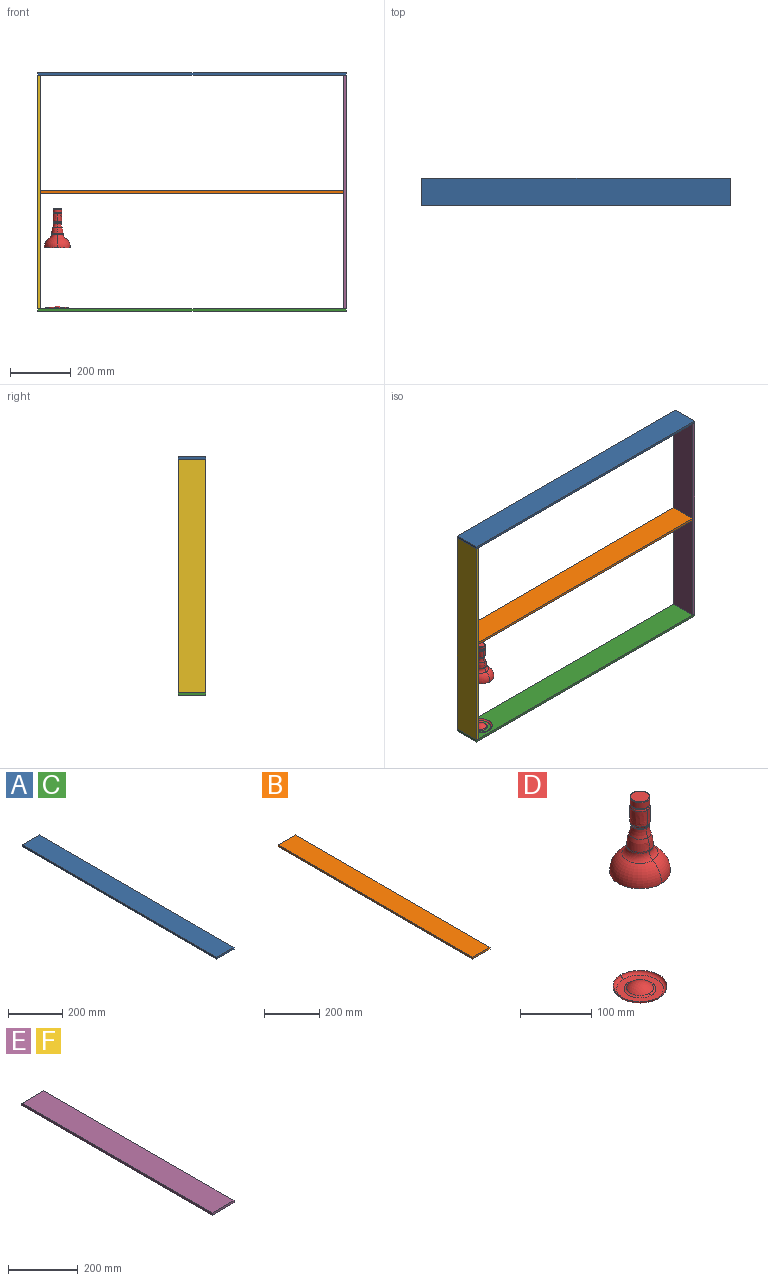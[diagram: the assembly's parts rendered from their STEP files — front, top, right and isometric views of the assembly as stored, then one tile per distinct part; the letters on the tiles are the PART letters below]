
ASSEMBLY  parts=6 mates=5
PART A: 6 faces, bbox 88.9x1016x7.9 mm
  f0: plane 1016x7.94mm, normal (-1,0,0), area 8064.5mm2, adj f1,f3,f4,f5
  f1: plane 88.9x7.94mm, normal (0,-1,0), area 705.6mm2, adj f0,f2,f4,f5
  f2: plane 1016x7.94mm, normal (1,0,0), area 8064.5mm2, adj f1,f3,f4,f5
  f3: plane 88.9x7.94mm, normal (0,1,0), area 705.6mm2, adj f0,f2,f4,f5
  f4: plane 1016x88.9mm, normal (0,0,1), area 90322.4mm2, adj f0,f1,f2,f3
  f5: plane 1016x88.9mm, normal (0,0,-1), area 90322.4mm2, adj f0,f1,f2,f3
PART B: 6 faces, bbox 88.9x1000.1x7.9 mm
  f0: plane 88.9x7.94mm, normal (0,-1,0), area 705.6mm2, adj f1,f3,f4,f5
  f1: plane 1000.13x7.94mm, normal (1,0,0), area 7938.5mm2, adj f0,f2,f4,f5
  f2: plane 88.9x7.94mm, normal (0,1,0), area 705.6mm2, adj f1,f3,f4,f5
  f3: plane 1000.13x7.94mm, normal (-1,0,0), area 7938.5mm2, adj f0,f2,f4,f5
  f4: plane 1000.13x88.9mm, normal (0,0,1), area 88911.1mm2, adj f0,f1,f2,f3
  f5: plane 1000.13x88.9mm, normal (0,0,-1), area 88911.1mm2, adj f0,f1,f2,f3
PART C: same geometry as A
PART D: 35 faces, bbox 84.8x84.9x333.9 mm
  f0: sphere r=25mm, area 833.3mm2, adj f1,f2
  f1: torus R=22.36mm, axis (0,0,1), area 269.2mm2, adj f0,f2,f3
  f2: torus R=22.36mm, axis (0,0,1), area 269.2mm2, adj f0,f1,f3
  f3: plane 65.68x65.68mm, normal (0,0,-1), area 1818.2mm2, adj f1,f2,f4,f5
  f4: torus R=32.84mm, axis (0,0,1), area 875mm2, adj f3,f5,f6
  f5: torus R=32.84mm, axis (0,0,1), area 875mm2, adj f3,f4,f6
  f6: cone r=0mm half-angle=1.3deg, axis (0,0,1), area 49622.5mm2, adj f4,f5,f7,f8
  f7: torus R=8.99mm, axis (0,0,1), area 4352mm2, adj f6,f8,f9
  f8: torus R=8.99mm, axis (0,0,1), area 4352mm2, adj f6,f7,f10
  f9: torus R=33.78mm, axis (0,0,1), area 970.6mm2, adj f7,f10,f11
  f10: torus R=33.78mm, axis (0,0,1), area 970.6mm2, adj f8,f9,f12
  f11: torus R=33.78mm, axis (0,0,1), area 134mm2, adj f9,f12,f13
  f12: torus R=33.78mm, axis (0,0,1), area 134mm2, adj f10,f11,f14
  f13: revolved ~37.65x19.38mm, area 1098.1mm2, adj f11,f14,f15
  f14: revolved ~37.65x19.38mm, area 1098.1mm2, adj f12,f13,f16
  f15: torus R=54.46mm, axis (0,0,1), area 655.5mm2, adj f13,f16,f17
  f16: torus R=54.46mm, axis (0,0,1), area 655.5mm2, adj f14,f15,f18
  f17: torus R=54.46mm, axis (0,0,1), area 56.6mm2, adj f15,f18,f19
  f18: torus R=54.46mm, axis (0,0,1), area 56.6mm2, adj f16,f17,f20
  f19: torus R=14.26mm, axis (0,0,1), area 28.3mm2, adj f17,f20,f21
  f20: torus R=14.26mm, axis (0,0,1), area 28.3mm2, adj f18,f19,f22
  f21: torus R=9.09mm, axis (0,0,-1), area 147mm2, adj f19,f22,f23
  f22: torus R=9.09mm, axis (0,0,-1), area 147mm2, adj f20,f21,f25
  f23: revolved ~28.46x26.15mm, area 1165.2mm2, adj f21,f25,f27
  f24: plane 25.92x25.92mm, normal (0,0,1), area 528.5mm2, adj f26,f28
  f25: revolved ~28.46x26.15mm, area 1165.2mm2, adj f22,f23,f29
  f26: torus R=12.96mm, axis (0,0,-1), area 67.1mm2, adj f24,f28,f31
  f27: torus R=9.08mm, axis (0,0,-1), area 127mm2, adj f23,f29,f30
  f28: torus R=12.96mm, axis (0,0,-1), area 67.1mm2, adj f24,f26,f31
  f29: torus R=9.08mm, axis (0,0,-1), area 127mm2, adj f25,f27,f32
  f30: torus R=14.34mm, axis (0,0,1), area 35.3mm2, adj f27,f32,f33
  f31: cylinder r=13.96mm len=27.92mm, axis (0,0,1), area 917.8mm2, adj f26,f28,f33,f34
  f32: torus R=14.34mm, axis (0,0,1), area 35.3mm2, adj f29,f30,f34
  f33: torus R=14.34mm, axis (0,0,1), area 76.5mm2, adj f30,f31,f34
  f34: torus R=14.34mm, axis (0,0,1), area 76.5mm2, adj f31,f32,f33
PART E: 6 faces, bbox 88.9x769.9x7.9 mm
  f0: plane 769.94x7.94mm, normal (-1,0,0), area 6111.4mm2, adj f1,f3,f4,f5
  f1: plane 88.9x7.94mm, normal (0,-1,0), area 705.6mm2, adj f0,f2,f4,f5
  f2: plane 769.94x7.94mm, normal (1,0,0), area 6111.4mm2, adj f1,f3,f4,f5
  f3: plane 88.9x7.94mm, normal (0,1,0), area 705.6mm2, adj f0,f2,f4,f5
  f4: plane 769.94x88.9mm, normal (0,0,1), area 68447.4mm2, adj f0,f1,f2,f3
  f5: plane 769.94x88.9mm, normal (0,0,-1), area 68447.4mm2, adj f0,f1,f2,f3
PART F: same geometry as E
PLACE A rot(axis=(0,0,-1),90deg) t=(0,88.9,777.88)mm
PLACE B rot(axis=(0,0,-1),90deg) t=(7.94,-88.9,388.94)mm
PLACE C rot(axis=(0,0,-1),90deg) t=(0,88.9,0)mm
PLACE D t=(64.85,44.45,7.94)mm
PLACE E rot(axis=(0.58,0.58,0.58),120deg) t=(1008.06,-177.8,7.94)mm
PLACE F rot(axis=(0.58,-0.58,-0.58),120deg) t=(7.94,266.7,7.94)mm
MATE fastened E.f1 <-> C.f4  axis (0,0,-1) through (1016,88.9,7.94)mm
MATE planar D.f30 <-> C.f4  axis (0,0,-1) through (64.85,44.45,7.94)mm
MATE fastened F.f1 <-> C.f4  axis (0,0,-1) through (0,88.9,7.94)mm
MATE fastened A.f5 <-> F.f3  axis (0,0,-1) through (0,0,777.88)mm
MATE fastened B.f0 <-> F.f5  axis (-1,0,0) through (7.94,0,388.94)mm
